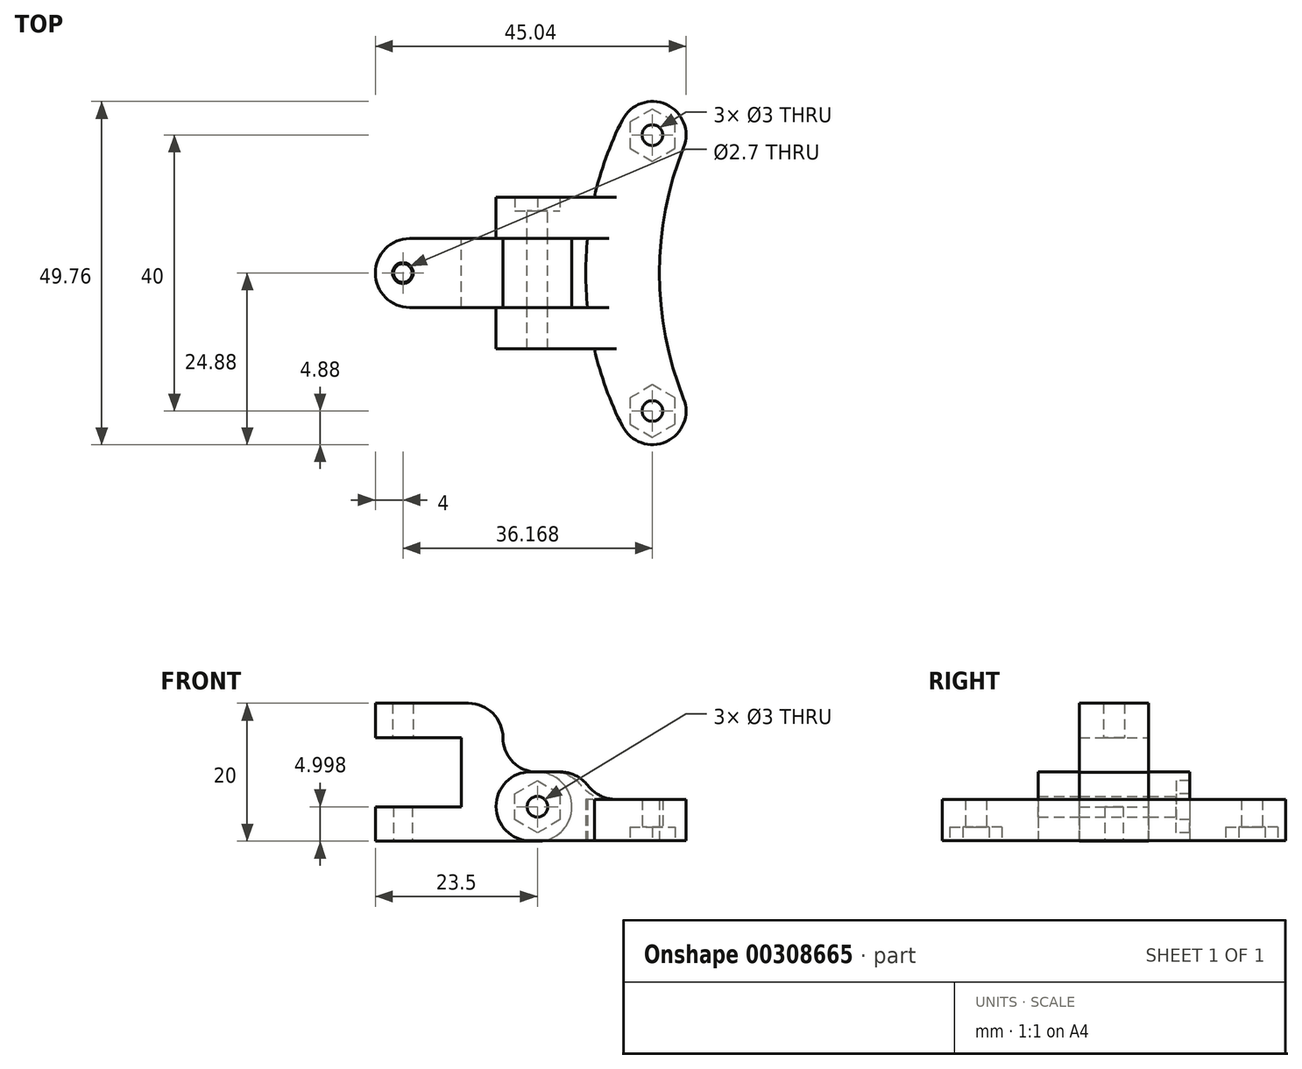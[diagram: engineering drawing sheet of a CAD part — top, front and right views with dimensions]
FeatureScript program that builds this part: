
annotation { "Feature Type Name" : "Feature", "Feature Type Description" : "" }
export const myFeature = defineFeature(function(context is Context, id is Id, definition is map)
    precondition{}
    {
        {
            var Q0;
            Q0=qCreatedBy(makeId("Front.planeOp"),FACE);
            var sketch = newSketch(context, id + "F0", { "sketchPlane" : qUnion([Q0])});
            skLineSegment(sketch, "E0.bottom", {"start": v(0, 21.94) * mm, "end": v(-12.5, 21.94) * mm});
            skLineSegment(sketch, "E0.top", {"start": v(0, 26.94) * mm, "end": v(-12.5, 26.94) * mm});
            skLineSegment(sketch, "E0.left", {"start": v(0, 21.94) * mm, "end": v(0, 26.94) * mm});
            skLineSegment(sketch, "E0.right", {"start": v(-12.5, 21.94) * mm, "end": v(-12.5, 26.94) * mm});
            skLineSegment(sketch, "E1.0", {"start": v(-8.5, 21.94) * mm, "end": v(-8.5, 26.94) * mm});
            skLineSegment(sketch, "E2.0", {"start": v(-10, 21.94) * mm, "end": v(-10, 26.94) * mm});
            skLineSegment(sketch, "E3.bottom", {"start": v(0, 6.94) * mm, "end": v(-12.5, 6.94) * mm});
            skLineSegment(sketch, "E3.top", {"start": v(0, 11.94) * mm, "end": v(-12.5, 11.94) * mm});
            skLineSegment(sketch, "E3.left", {"start": v(0, 6.94) * mm, "end": v(0, 11.94) * mm});
            skLineSegment(sketch, "E3.right", {"start": v(-12.5, 6.94) * mm, "end": v(-12.5, 11.94) * mm});
            skLineSegment(sketch, "E4.0", {"start": v(-8.5, 6.94) * mm, "end": v(-8.5, 11.94) * mm});
            skLineSegment(sketch, "E5.0", {"start": v(-9.85, 6.94) * mm, "end": v(-9.85, 11.94) * mm});
            skLineSegment(sketch, "E6.bottom", {"start": v(0, 26.94) * mm, "end": v(6, 26.94) * mm});
            skLineSegment(sketch, "E6.top", {"start": v(0, 6.94) * mm, "end": v(6, 6.94) * mm});
            skLineSegment(sketch, "E6.left", {"start": v(0, 26.94) * mm, "end": v(0, 6.94) * mm});
            skLineSegment(sketch, "E6.right", {"start": v(6, 26.94) * mm, "end": v(6, 6.94) * mm});
            skLineSegment(sketch, "E7.bottom", {"start": v(6, 6.94) * mm, "end": v(16, 6.94) * mm});
            skLineSegment(sketch, "E7.top", {"start": v(6, 16.94) * mm, "end": v(16, 16.94) * mm});
            skLineSegment(sketch, "E7.left", {"start": v(6, 6.94) * mm, "end": v(6, 16.94) * mm});
            skLineSegment(sketch, "E7.right", {"start": v(16, 6.94) * mm, "end": v(16, 16.94) * mm});
            skCircle(sketch, "E8", {"center": v(11, 11.94) * mm, "radius": 1.5 * mm});
            skCircle(sketch, "E9.cCircle", {"center": v(11, 11.94) * mm, "radius": 3.28 * mm, "construction": true});
            skLineSegment(sketch, "E9.0", {"start": v(14.28, 13.83) * mm, "end": v(14.28, 10.05) * mm});
            skLineSegment(sketch, "E9.1", {"start": v(14.28, 10.05) * mm, "end": v(11, 8.16) * mm});
            skLineSegment(sketch, "E9.2", {"start": v(11, 8.16) * mm, "end": v(7.73, 10.05) * mm});
            skLineSegment(sketch, "E9.3", {"start": v(7.73, 10.05) * mm, "end": v(7.73, 13.83) * mm});
            skLineSegment(sketch, "E9.4", {"start": v(7.72, 13.83) * mm, "end": v(11, 15.72) * mm});
            skLineSegment(sketch, "E9.5", {"start": v(11, 15.72) * mm, "end": v(14.28, 13.83) * mm});
            skPoint(sketch, "E9.0.midPoint", {"position": v(14.28, 11.94) * mm});
            skSolve(sketch);
        }
        {
            var Q0;
            {var subQ3=sQuery(id+"F0.wireOp",EDGE,"E6.bottom");Q0=makeQuery(id+"F0.imprint","IMPRINT",FACE,{"disambiguationData":[TD([[makeQuery(id+"F0.imprint","IMPRINT",EDGE,{"derivedFrom":subQ3}),-1.0]])]});}
            var Q1;
            {var subQ3=sQuery(id+"F0.wireOp",EDGE,"E4.0");Q1=makeQuery(id+"F0.imprint","IMPRINT",FACE,{"disambiguationData":[TD([[makeQuery(id+"F0.imprint","IMPRINT",EDGE,{"derivedFrom":subQ3}),-1.0]])]});}
            var Q2;
            {var subQ4=sQuery(id+"F0.wireOp",EDGE,"E0.top");Q2=makeQuery(id+"F0.imprint","IMPRINT",FACE,{"disambiguationData":[TD([[makeQuery(id+"F0.imprint","IMPRINT",EDGE,{"derivedFrom":subQ4}),1.0]])]});}
            var Q3;
            {var subQ0=sQuery(id+"F0.wireOp",EDGE,"E3.right");Q3=makeQuery(id+"F0.imprint","IMPRINT",FACE,{"disambiguationData":[TD([[makeQuery(id+"F0.imprint","IMPRINT",EDGE,{"derivedFrom":subQ0}),-1.0]])]});}
            var Q4;
            {var subQ0=sQuery(id+"F0.wireOp",EDGE,"E4.0");Q4=makeQuery(id+"F0.imprint","IMPRINT",FACE,{"disambiguationData":[TD([[makeQuery(id+"F0.imprint","IMPRINT",EDGE,{"derivedFrom":subQ0}),1.0]])]});}
            var Q5;
            Q5=makeQuery(id+"F0.imprint","IMPRINT",FACE,{"disambiguationData":[TD([[makeQuery(id+"F0.imprint","IMPRINT",EDGE,{"derivedFrom":sQuery(id+"F0.wireOp",EDGE,"E7.bottom")}),1.0]])]});
            var Q6;
            Q6=makeQuery(id+"F0.imprint","IMPRINT",FACE,{"disambiguationData":[TD([[makeQuery(id+"F0.imprint","IMPRINT",EDGE,{"derivedFrom":sQuery(id+"F0.wireOp",EDGE,"E8")}),-1.0]])]});
            extrude(context, id + "F1", {"entities" : qUnion([Q0, Q1, Q2, Q3, Q4, Q5, Q6]), "depth" : 10 * mm});
        }
        {
            var Q0;
            Q0=makeQuery(id+"F1.opExtrude","CAP_EDGE",EDGE,{"disambiguationData":[OSD([sQuery(id+"F0.wireOp",EDGE,"E0.right")])],"isStart":false});
            var Q1;
            Q1=makeQuery(id+"F1.opExtrude","CAP_EDGE",EDGE,{"disambiguationData":[OSD([sQuery(id+"F0.wireOp",EDGE,"E0.right")])],"isStart":true});
            var Q2;
            Q2=makeQuery(id+"F1.opExtrude","CAP_EDGE",EDGE,{"disambiguationData":[OSD([sQuery(id+"F0.wireOp",EDGE,"E3.right")])],"isStart":true});
            var Q3;
            Q3=makeQuery(id+"F1.opExtrude","CAP_EDGE",EDGE,{"disambiguationData":[OSD([sQuery(id+"F0.wireOp",EDGE,"E3.right")])],"isStart":false});
            var Q4;
            Q4=makeQuery(id+"F1.opExtrude","SWEPT_EDGE",EDGE,{"disambiguationData":[OSD([sQuery(id+"F0.wireOp",EDGE,"E7.top"),sQuery(id+"F0.wireOp",EDGE,"E7.right")])]});
            var Q5;
            Q5=makeQuery(id+"F1.opExtrude","SWEPT_EDGE",EDGE,{"disambiguationData":[OSD([sQuery(id+"F0.wireOp",EDGE,"E7.bottom"),sQuery(id+"F0.wireOp",EDGE,"E7.right")])]});
            fillet(context, id + "F2", {"entities" : qUnion([Q0, Q1, Q2, Q3, Q4, Q5]), "radius" : 5 * mm, "tangentPropagation" : true, "allowEdgeOverflow" : false});
        }
        {
            var Q0;
            {var subQ0=sQuery(id+"F0.wireOp",EDGE,"E1.0");Q0=makeQuery(id+"F0.imprint","IMPRINT",FACE,{"disambiguationData":[TD([[makeQuery(id+"F0.imprint","IMPRINT",EDGE,{"derivedFrom":subQ0}),1.0]])]});}
            var Q1;
            Q1=sQuery(id+"F0.wireOp",EDGE,"E1.0");
            revolve(context, id + "F3", {"entities" : qUnion([Q0]), "axis" : qUnion([Q1]), "revolveType" : RevolveType.FULL});
        }
        {
            var Q0;
            {var subQ0=sQuery(id+"F0.wireOp",EDGE,"E4.0");Q0=makeQuery(id+"F0.imprint","IMPRINT",FACE,{"disambiguationData":[TD([[makeQuery(id+"F0.imprint","IMPRINT",EDGE,{"derivedFrom":subQ0}),1.0]])]});}
            var Q1;
            Q1=sQuery(id+"F0.wireOp",EDGE,"E4.0");
            revolve(context, id + "F4", {"entities" : qUnion([Q0]), "axis" : qUnion([Q1]), "revolveType" : RevolveType.FULL});
        }
        {
            var Q0;
            Q0=makeQuery(id+"F3.opRevolve","SWEPT_BODY",BODY,{"disambiguationData":[OSD([sQuery(id+"F0.wireOp",EDGE,"E0.bottom"),sQuery(id+"F0.wireOp",EDGE,"E0.top"),sQuery(id+"F0.wireOp",EDGE,"E1.0"),sQuery(id+"F0.wireOp",EDGE,"E2.0")])]});
            var Q1;
            Q1=makeQuery(id+"F4.opRevolve","SWEPT_BODY",BODY,{"disambiguationData":[OSD([sQuery(id+"F0.wireOp",EDGE,"E3.bottom"),sQuery(id+"F0.wireOp",EDGE,"E3.top"),sQuery(id+"F0.wireOp",EDGE,"E4.0"),sQuery(id+"F0.wireOp",EDGE,"E5.0")])]});
            transform(context, id + "F5", {"entities" : qUnion([Q0, Q1]), "transformType" : TransformType.TRANSLATION_3D, "dx" : 0 * mm, "dy" : -5 * mm, "dz" : 0 * mm, "makeCopy" : false});
        }
        {
            var Q0;
            Q0=makeQuery(id+"F3.opRevolve","SWEPT_BODY",BODY,{"disambiguationData":[OSD([sQuery(id+"F0.wireOp",EDGE,"E0.bottom"),sQuery(id+"F0.wireOp",EDGE,"E0.top"),sQuery(id+"F0.wireOp",EDGE,"E1.0"),sQuery(id+"F0.wireOp",EDGE,"E2.0")])]});
            var Q1;
            Q1=makeQuery(id+"F4.opRevolve","SWEPT_BODY",BODY,{"disambiguationData":[OSD([sQuery(id+"F0.wireOp",EDGE,"E3.bottom"),sQuery(id+"F0.wireOp",EDGE,"E3.top"),sQuery(id+"F0.wireOp",EDGE,"E4.0"),sQuery(id+"F0.wireOp",EDGE,"E5.0")])]});
            var Q2;
            Q2=makeQuery(id+"F1.opExtrude","SWEPT_BODY",BODY,{"disambiguationData":[OSD([sQuery(id+"F0.wireOp",EDGE,"E0.bottom"),sQuery(id+"F0.wireOp",EDGE,"E0.top"),sQuery(id+"F0.wireOp",EDGE,"E0.right"),sQuery(id+"F0.wireOp",EDGE,"E3.bottom"),sQuery(id+"F0.wireOp",EDGE,"E3.top"),sQuery(id+"F0.wireOp",EDGE,"E3.right"),sQuery(id+"F0.wireOp",EDGE,"E6.bottom"),sQuery(id+"F0.wireOp",EDGE,"E6.top"),sQuery(id+"F0.wireOp",EDGE,"E6.left"),sQuery(id+"F0.wireOp",EDGE,"E6.right"),sQuery(id+"F0.wireOp",EDGE,"E7.bottom"),sQuery(id+"F0.wireOp",EDGE,"E7.top"),sQuery(id+"F0.wireOp",EDGE,"E7.right"),sQuery(id+"F0.wireOp",EDGE,"E8")])]});
            booleanBodies(context, id + "F6", {"operationType" : BooleanOperationType.SUBTRACTION, "tools" : qUnion([Q0, Q1]), "targets" : qUnion([Q2])});
        }
        {
            var Q0;
            Q0=qCreatedBy(makeId("Top.planeOp"),FACE);
            var sketch = newSketch(context, id + "F7", { "sketchPlane" : qUnion([Q0])});
            skCircle(sketch, "E10", {"center": v(27.67, 15) * mm, "radius": 1.5 * mm});
            skCircle(sketch, "E11", {"center": v(27.67, -25) * mm, "radius": 1.5 * mm});
            skCircle(sketch, "E12", {"center": v(27.67, 15) * mm, "radius": 4.88 * mm});
            skCircle(sketch, "E13", {"center": v(27.67, -25) * mm, "radius": 4.88 * mm});
            skArc(sketch, "E14", {"start": v(32.2, 13.2) * mm, "mid": v(28.7, -5) * mm, "end": v(32.2, -23.2) * mm});
            skArc(sketch, "E15", {"start": v(23.32, 17.2) * mm, "mid": v(18, -5) * mm, "end": v(23.32, -27.2) * mm});
            skLineSegment(sketch, "E16.bottom", {"start": v(22, 0) * mm, "end": v(5, 0) * mm});
            skLineSegment(sketch, "E16.top", {"start": v(22, 6) * mm, "end": v(5, 6) * mm});
            skLineSegment(sketch, "E16.left", {"start": v(22, 0) * mm, "end": v(22, 6) * mm});
            skLineSegment(sketch, "E16.right", {"start": v(5, 0) * mm, "end": v(5, 6) * mm});
            skLineSegment(sketch, "E17.bottom", {"start": v(22, -16) * mm, "end": v(5, -16) * mm});
            skLineSegment(sketch, "E17.top", {"start": v(22, -10) * mm, "end": v(5, -10) * mm});
            skLineSegment(sketch, "E17.left", {"start": v(22, -16) * mm, "end": v(22, -10) * mm});
            skLineSegment(sketch, "E17.right", {"start": v(5, -16) * mm, "end": v(5, -10) * mm});
            skCircle(sketch, "E18.cCircle", {"center": v(27.67, 15) * mm, "radius": 3.28 * mm, "construction": true});
            skLineSegment(sketch, "E18.0", {"start": v(30.94, 16.9) * mm, "end": v(30.94, 13.1) * mm});
            skLineSegment(sketch, "E18.1", {"start": v(30.94, 13.1) * mm, "end": v(27.67, 11.22) * mm});
            skLineSegment(sketch, "E18.2", {"start": v(27.67, 11.22) * mm, "end": v(24.4, 13.1) * mm});
            skLineSegment(sketch, "E18.3", {"start": v(24.4, 13.1) * mm, "end": v(24.4, 16.9) * mm});
            skLineSegment(sketch, "E18.4", {"start": v(24.4, 16.9) * mm, "end": v(27.67, 18.78) * mm});
            skLineSegment(sketch, "E18.5", {"start": v(27.67, 18.78) * mm, "end": v(30.94, 16.9) * mm});
            skPoint(sketch, "E18.0.midPoint", {"position": v(30.94, 15) * mm});
            skCircle(sketch, "E19.cCircle", {"center": v(27.67, -25) * mm, "radius": 3.28 * mm, "construction": true});
            skLineSegment(sketch, "E19.0", {"start": v(30.94, -23.1) * mm, "end": v(30.94, -26.9) * mm});
            skLineSegment(sketch, "E19.1", {"start": v(30.94, -26.9) * mm, "end": v(27.67, -28.78) * mm});
            skLineSegment(sketch, "E19.2", {"start": v(27.67, -28.78) * mm, "end": v(24.4, -26.9) * mm});
            skLineSegment(sketch, "E19.3", {"start": v(24.4, -26.9) * mm, "end": v(24.4, -23.1) * mm});
            skLineSegment(sketch, "E19.4", {"start": v(24.4, -23.1) * mm, "end": v(27.67, -21.22) * mm});
            skLineSegment(sketch, "E19.5", {"start": v(27.67, -21.22) * mm, "end": v(30.94, -23.1) * mm});
            skPoint(sketch, "E19.0.midPoint", {"position": v(30.94, -25) * mm});
            skSolve(sketch);
        }
        {
            var Q0;
            {var subQ5=sQuery(id+"F7.wireOp",EDGE,"E17.right");Q0=makeQuery(id+"F7.imprint","IMPRINT",FACE,{"disambiguationData":[TD([[makeQuery(id+"F7.imprint","IMPRINT",EDGE,{"derivedFrom":subQ5}),-1.0]])]});}
            var Q1;
            {var subQ5=sQuery(id+"F7.wireOp",EDGE,"E16.right");Q1=makeQuery(id+"F7.imprint","IMPRINT",FACE,{"disambiguationData":[TD([[makeQuery(id+"F7.imprint","IMPRINT",EDGE,{"derivedFrom":subQ5}),-1.0]])]});}
            extrude(context, id + "F8", {"entities" : qUnion([Q0, Q1]), "depth" : 17 * mm, "hasSecondDirection" : true, "secondDirectionOppositeDirection" : false, "secondDirectionDepth" : 7 * mm});
        }
        {
            var Q0;
            Q0=makeQuery(id+"F7.imprint","IMPRINT",FACE,{"disambiguationData":[TD([[makeQuery(id+"F7.imprint","IMPRINT",EDGE,{"derivedFrom":sQuery(id+"F7.wireOp",EDGE,"E11")}),-1.0]])]});
            var Q1;
            {var subQ12=sQuery(id+"F7.wireOp",EDGE,"E14");Q1=makeQuery(id+"F7.imprint","IMPRINT",FACE,{"disambiguationData":[TD([[makeQuery(id+"F7.imprint","IMPRINT",EDGE,{"derivedFrom":subQ12}),-1.0]])]});}
            var Q2;
            Q2=makeQuery(id+"F7.imprint","IMPRINT",FACE,{"disambiguationData":[TD([[makeQuery(id+"F7.imprint","IMPRINT",EDGE,{"derivedFrom":sQuery(id+"F7.wireOp",EDGE,"E10")}),-1.0]])]});
            var Q3;
            {var subQ5=sQuery(id+"F7.wireOp",EDGE,"E17.left");Q3=makeQuery(id+"F7.imprint","IMPRINT",FACE,{"disambiguationData":[TD([[makeQuery(id+"F7.imprint","IMPRINT",EDGE,{"derivedFrom":subQ5}),1.0]])]});}
            var Q4;
            {var subQ5=sQuery(id+"F7.wireOp",EDGE,"E16.left");Q4=makeQuery(id+"F7.imprint","IMPRINT",FACE,{"disambiguationData":[TD([[makeQuery(id+"F7.imprint","IMPRINT",EDGE,{"derivedFrom":subQ5}),1.0]])]});}
            var Q5;
            Q5=makeQuery(id+"F7.imprint","IMPRINT",FACE,{"disambiguationData":[TD([[makeQuery(id+"F7.imprint","IMPRINT",EDGE,{"derivedFrom":sQuery(id+"F7.wireOp",EDGE,"E18.0")}),1.0]])]});
            var Q6;
            Q6=makeQuery(id+"F7.imprint","IMPRINT",FACE,{"disambiguationData":[TD([[makeQuery(id+"F7.imprint","IMPRINT",EDGE,{"derivedFrom":sQuery(id+"F7.wireOp",EDGE,"E19.0")}),1.0]])]});
            extrude(context, id + "F9", {"entities" : qUnion([Q0, Q1, Q2, Q3, Q4, Q5, Q6]), "operationType" : NewBodyOperationType.ADD, "depth" : 13 * mm, "hasSecondDirection" : true, "secondDirectionOppositeDirection" : false, "secondDirectionDepth" : 7 * mm});
        }
        {
            var Q0;
            {var subQ0=sQuery(id+"F7.wireOp",EDGE,"E15");Q0=makeQuery(id+"F8.opExtrude","CAP_EDGE",EDGE,{"disambiguationData":[OSD([subQ0]),TDD([makeQuery(id+"F7.imprint","IMPRINT",EDGE,{"disambiguationData":[TD([[makeQuery(id+"F7.imprint","INTERSECT",VERTEX,{"derivedFrom":[subQ0,sQuery(id+"F7.wireOp",EDGE,"E17.top")]}),-1.0]])],"derivedFrom":subQ0})])],"isStart":false});}
            var Q1;
            {var subQ0=sQuery(id+"F7.wireOp",EDGE,"E15");Q1=makeQuery(id+"F8.opExtrude","CAP_EDGE",EDGE,{"disambiguationData":[OSD([subQ0]),TDD([makeQuery(id+"F7.imprint","IMPRINT",EDGE,{"disambiguationData":[TD([[makeQuery(id+"F7.imprint","INTERSECT",VERTEX,{"derivedFrom":[subQ0,sQuery(id+"F7.wireOp",EDGE,"E16.top")]}),-1.0]])],"derivedFrom":subQ0})])],"isStart":false});}
            var Q2;
            {var subQ0=sQuery(id+"F7.wireOp",EDGE,"E15");Q2=makeQuery(id+"F8.opExtrude","CAP_EDGE",EDGE,{"disambiguationData":[OSD([subQ0]),TDD([makeQuery(id+"F7.imprint","IMPRINT",EDGE,{"disambiguationData":[TD([[makeQuery(id+"F7.imprint","INTERSECT",VERTEX,{"derivedFrom":[subQ0,sQuery(id+"F7.wireOp",EDGE,"E17.top")]}),-1.0]])],"derivedFrom":subQ0})])],"isStart":true});}
            var Q3;
            {var subQ0=sQuery(id+"F7.wireOp",EDGE,"E15");Q3=makeQuery(id+"F8.opExtrude","CAP_EDGE",EDGE,{"disambiguationData":[OSD([subQ0]),TDD([makeQuery(id+"F7.imprint","IMPRINT",EDGE,{"disambiguationData":[TD([[makeQuery(id+"F7.imprint","INTERSECT",VERTEX,{"derivedFrom":[subQ0,sQuery(id+"F7.wireOp",EDGE,"E16.top")]}),-1.0]])],"derivedFrom":subQ0})])],"isStart":true});}
            var Q4;
            Q4=makeQuery(id+"F8.opExtrude","CAP_EDGE",EDGE,{"disambiguationData":[OSD([sQuery(id+"F7.wireOp",EDGE,"E17.right")])],"isStart":false});
            var Q5;
            Q5=makeQuery(id+"F8.opExtrude","CAP_EDGE",EDGE,{"disambiguationData":[OSD([sQuery(id+"F7.wireOp",EDGE,"E17.right")])],"isStart":true});
            var Q6;
            Q6=makeQuery(id+"F8.opExtrude","CAP_EDGE",EDGE,{"disambiguationData":[OSD([sQuery(id+"F7.wireOp",EDGE,"E16.right")])],"isStart":true});
            var Q7;
            Q7=makeQuery(id+"F8.opExtrude","CAP_EDGE",EDGE,{"disambiguationData":[OSD([sQuery(id+"F7.wireOp",EDGE,"E16.right")])],"isStart":false});
            fillet(context, id + "F10", {"entities" : qUnion([Q0, Q1, Q2, Q3, Q4, Q5, Q6, Q7]), "radius" : 5 * mm, "tangentPropagation" : true, "allowEdgeOverflow" : false});
        }
        {
            var Q0;
            Q0=makeQuery(id+"F0.imprint","IMPRINT",FACE,{"disambiguationData":[TD([[makeQuery(id+"F0.imprint","IMPRINT",EDGE,{"derivedFrom":sQuery(id+"F0.wireOp",EDGE,"E8")}),1.0]])]});
            extrude(context, id + "F11", {"entities" : qUnion([Q0]), "operationType" : NewBodyOperationType.REMOVE, "depth" : 25 * mm, "hasSecondDirection" : true, "secondDirectionOppositeDirection" : true, "secondDirectionDepth" : 25 * mm});
        }
        {
            var Q0;
            Q0=makeQuery(id+"F0.imprint","IMPRINT",FACE,{"disambiguationData":[TD([[makeQuery(id+"F0.imprint","IMPRINT",EDGE,{"derivedFrom":sQuery(id+"F0.wireOp",EDGE,"E8")}),-1.0]])]});
            extrude(context, id + "F12", {"entities" : qUnion([Q0]), "operationType" : NewBodyOperationType.REMOVE, "oppositeDirection" : true, "depth" : 10 * mm, "hasSecondDirection" : true, "secondDirectionOppositeDirection" : true, "secondDirectionDepth" : 4 * mm});
        }
        {
            var Q0;
            Q0=makeQuery(id+"F7.imprint","IMPRINT",FACE,{"disambiguationData":[TD([[makeQuery(id+"F7.imprint","IMPRINT",EDGE,{"derivedFrom":sQuery(id+"F7.wireOp",EDGE,"E11")}),-1.0]])]});
            var Q1;
            Q1=makeQuery(id+"F7.imprint","IMPRINT",FACE,{"disambiguationData":[TD([[makeQuery(id+"F7.imprint","IMPRINT",EDGE,{"derivedFrom":sQuery(id+"F7.wireOp",EDGE,"E10")}),-1.0]])]});
            extrude(context, id + "F13", {"entities" : qUnion([Q0, Q1]), "operationType" : NewBodyOperationType.REMOVE, "depth" : 9 * mm});
        }
        {
            var Q0;
            {var subQ0=sQuery(id+"F7.wireOp",EDGE,"E15");Q0=makeQuery(id+"F10.opFillet","BLEND_EDGE",EDGE,{"blendedFrom":[makeQuery(id+"F8.opExtrude","CAP_EDGE",EDGE,{"disambiguationData":[OSD([subQ0]),TDD([makeQuery(id+"F7.imprint","IMPRINT",EDGE,{"disambiguationData":[TD([[makeQuery(id+"F7.imprint","INTERSECT",VERTEX,{"derivedFrom":[subQ0,sQuery(id+"F7.wireOp",EDGE,"E17.top")]}),-1.0]])],"derivedFrom":subQ0})])],"isStart":false}),makeQuery(id+"F9.opExtrude","CAP_FACE",FACE,{"disambiguationData":[OSD([sQuery(id+"F7.wireOp",EDGE,"E10"),sQuery(id+"F7.wireOp",EDGE,"E11"),sQuery(id+"F7.wireOp",EDGE,"E12"),sQuery(id+"F7.wireOp",EDGE,"E13"),sQuery(id+"F7.wireOp",EDGE,"E14"),subQ0])],"isStart":false})],"blendedInto":[makeQuery(id+"F9.opExtrude","CAP_FACE",FACE,{"disambiguationData":[OSD([sQuery(id+"F7.wireOp",EDGE,"E10"),sQuery(id+"F7.wireOp",EDGE,"E11"),sQuery(id+"F7.wireOp",EDGE,"E12"),sQuery(id+"F7.wireOp",EDGE,"E13"),sQuery(id+"F7.wireOp",EDGE,"E14"),subQ0])],"isStart":false})]});}
            var Q1;
            {var subQ0=sQuery(id+"F7.wireOp",EDGE,"E15");Q1=makeQuery(id+"F10.opFillet","BLEND_EDGE",EDGE,{"blendedFrom":[makeQuery(id+"F8.opExtrude","CAP_EDGE",EDGE,{"disambiguationData":[OSD([subQ0]),TDD([makeQuery(id+"F7.imprint","IMPRINT",EDGE,{"disambiguationData":[TD([[makeQuery(id+"F7.imprint","INTERSECT",VERTEX,{"derivedFrom":[subQ0,sQuery(id+"F7.wireOp",EDGE,"E16.top")]}),-1.0]])],"derivedFrom":subQ0})])],"isStart":false}),makeQuery(id+"F9.opExtrude","CAP_FACE",FACE,{"disambiguationData":[OSD([sQuery(id+"F7.wireOp",EDGE,"E10"),sQuery(id+"F7.wireOp",EDGE,"E11"),sQuery(id+"F7.wireOp",EDGE,"E12"),sQuery(id+"F7.wireOp",EDGE,"E13"),sQuery(id+"F7.wireOp",EDGE,"E14"),subQ0])],"isStart":false})],"blendedInto":[makeQuery(id+"F9.opExtrude","CAP_FACE",FACE,{"disambiguationData":[OSD([sQuery(id+"F7.wireOp",EDGE,"E10"),sQuery(id+"F7.wireOp",EDGE,"E11"),sQuery(id+"F7.wireOp",EDGE,"E12"),sQuery(id+"F7.wireOp",EDGE,"E13"),sQuery(id+"F7.wireOp",EDGE,"E14"),subQ0])],"isStart":false})]});}
            fillet(context, id + "F14", {"entities" : qUnion([Q0, Q1]), "radius" : 5 * mm, "tangentPropagation" : true, "allowEdgeOverflow" : false});
        }
        {
            var Q0;
            Q0=makeQuery(id+"F1.opExtrude","SWEPT_EDGE",EDGE,{"disambiguationData":[OSD([sQuery(id+"F0.wireOp",EDGE,"E6.bottom"),sQuery(id+"F0.wireOp",EDGE,"E6.right")])]});
            var Q1;
            Q1=makeQuery(id+"F1.opExtrude","SWEPT_EDGE",EDGE,{"disambiguationData":[OSD([sQuery(id+"F0.wireOp",EDGE,"E6.right"),sQuery(id+"F0.wireOp",EDGE,"E7.top"),sQuery(id+"F0.wireOp",EDGE,"E7.left")])]});
            fillet(context, id + "F15", {"entities" : qUnion([Q0, Q1]), "radius" : 5 * mm, "tangentPropagation" : true, "allowEdgeOverflow" : false});
        }
    });
